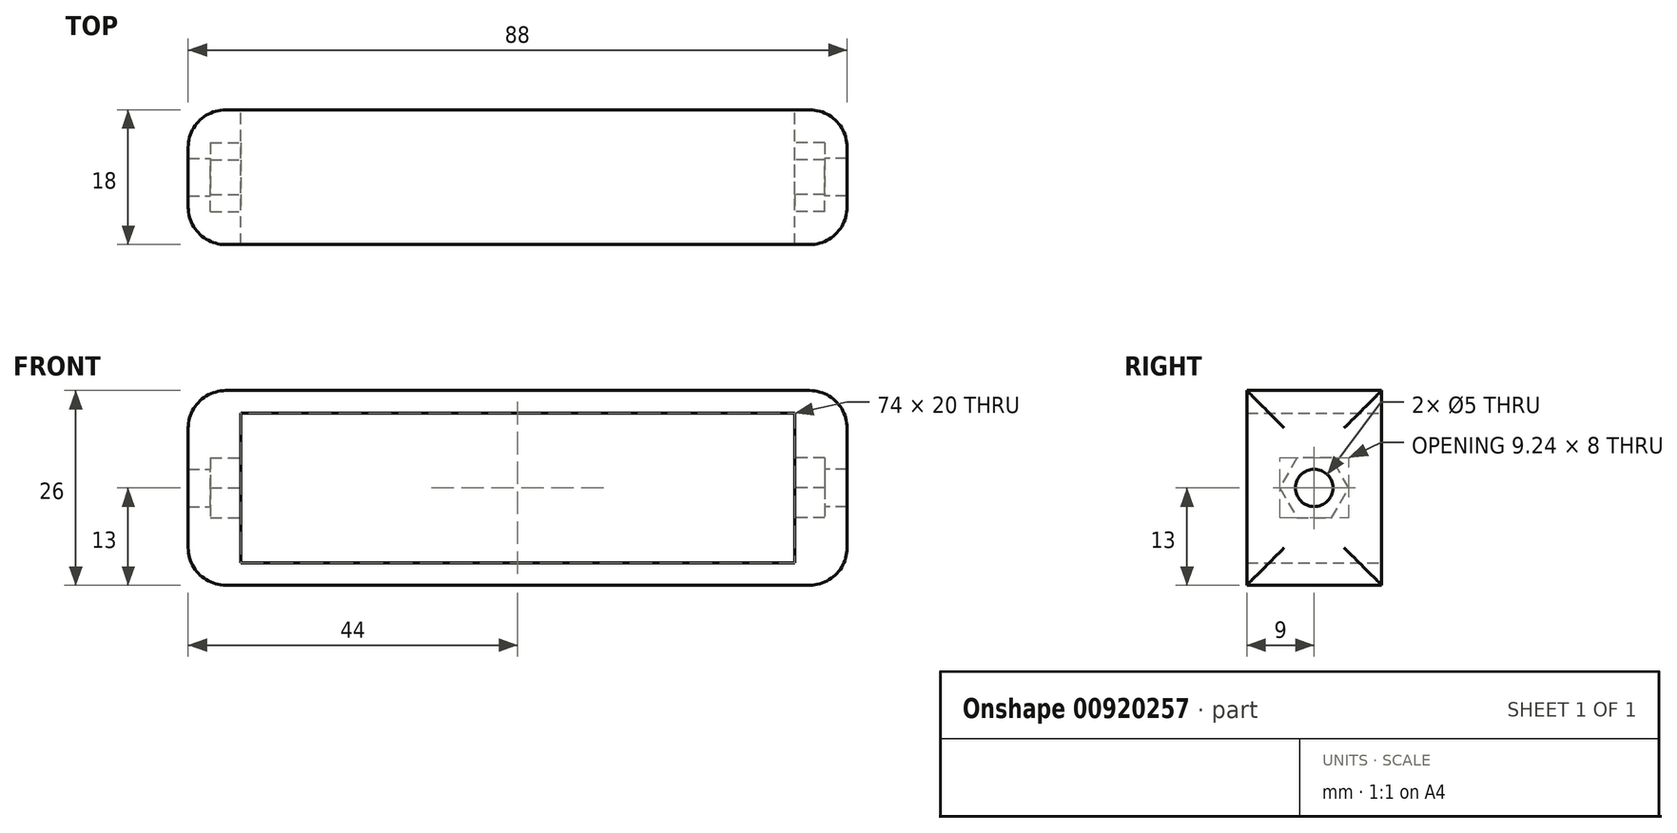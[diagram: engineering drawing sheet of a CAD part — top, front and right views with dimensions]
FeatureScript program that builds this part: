
annotation { "Feature Type Name" : "Feature", "Feature Type Description" : "" }
export const myFeature = defineFeature(function(context is Context, id is Id, definition is map)
    precondition{}
    {
        {
            var Q0;
            Q0=qCreatedBy(makeId("Top.planeOp"),FACE);
            var sketch = newSketch(context, id + "F0", { "sketchPlane" : qUnion([Q0])});
            skLineSegment(sketch, "E0.bottom", {"start": v(44, -9) * mm, "end": v(-44, -9) * mm});
            skLineSegment(sketch, "E0.top", {"start": v(44, 9) * mm, "end": v(-44, 9) * mm});
            skLineSegment(sketch, "E0.left", {"start": v(44, -9) * mm, "end": v(44, 9) * mm});
            skLineSegment(sketch, "E0.right", {"start": v(-44, -9) * mm, "end": v(-44, 9) * mm});
            skPoint(sketch, "E0.middle", {"position": v(0, 0) * mm});
            skSolve(sketch);
        }
        {
            var Q0;
            Q0 = qSketchRegion(id + "F0", true);
            extrude(context, id + "F1", {"entities" : qUnion([Q0]), "depth" : 23 * mm, "offsetDistance" : 25 * mm});
        }
        {
            var Q0;
            Q0=makeQuery(id+"F1.opExtrude","CAP_FACE",FACE,{"disambiguationData":[OSD([sQuery(id+"F0.wireOp",EDGE,"E0.bottom"),sQuery(id+"F0.wireOp",EDGE,"E0.top"),sQuery(id+"F0.wireOp",EDGE,"E0.left"),sQuery(id+"F0.wireOp",EDGE,"E0.right")])],"isStart":false});
            var sketch = newSketch(context, id + "F2", { "sketchPlane" : qUnion([Q0])});
            skLineSegment(sketch, "E1.bottom", {"start": v(37, -9) * mm, "end": v(-37, -9) * mm});
            skLineSegment(sketch, "E1.top", {"start": v(37, 9) * mm, "end": v(-37, 9) * mm});
            skLineSegment(sketch, "E1.left", {"start": v(37, -9) * mm, "end": v(37, 9) * mm});
            skLineSegment(sketch, "E1.right", {"start": v(-37, -9) * mm, "end": v(-37, 9) * mm});
            skPoint(sketch, "E1.middle", {"position": v(0, 0) * mm});
            skSolve(sketch);
        }
        {
            var Q0;
            Q0 = qSketchRegion(id + "F2", true);
            extrude(context, id + "F3", {"entities" : qUnion([Q0]), "operationType" : NewBodyOperationType.REMOVE, "oppositeDirection" : true, "depth" : 20 * mm, "offsetDistance" : 25 * mm});
        }
        {
            var Q0;
            Q0=makeQuery(id+"F3.boolean.opBoolean","COPY",FACE,{"derivedFrom":makeQuery(id+"F3.opExtrude","SWEPT_FACE",FACE,{"disambiguationData":[OSD([sQuery(id+"F2.wireOp",EDGE,"E1.right")])]})});
            var sketch = newSketch(context, id + "F4", { "sketchPlane" : qUnion([Q0])});
            skCircle(sketch, "E2.cCircle", {"center": v(0, 13) * mm, "radius": 4 * mm, "construction": true});
            skPoint(sketch, "E2.cCircle.centerSnap0", {"position": v(0, 23) * mm});
            skPoint(sketch, "E2.cCircle.centerSnap1", {"position": v(-9, 13) * mm});
            skLineSegment(sketch, "E2.0", {"start": v(2.3, 9) * mm, "end": v(-2.3, 9) * mm});
            skLineSegment(sketch, "E2.1", {"start": v(-2.3, 9) * mm, "end": v(-4.62, 13) * mm});
            skLineSegment(sketch, "E2.2", {"start": v(-4.62, 13) * mm, "end": v(-2.3, 17) * mm});
            skLineSegment(sketch, "E2.3", {"start": v(-2.3, 17) * mm, "end": v(2.3, 17) * mm});
            skLineSegment(sketch, "E2.4", {"start": v(2.3, 17) * mm, "end": v(4.62, 13) * mm});
            skLineSegment(sketch, "E2.5", {"start": v(4.62, 13) * mm, "end": v(2.3, 9) * mm});
            skPoint(sketch, "E2.0.midPoint", {"position": v(0, 9) * mm});
            skSolve(sketch);
        }
        {
            var Q0;
            Q0 = qSketchRegion(id + "F4", true);
            extrude(context, id + "F5", {"entities" : qUnion([Q0]), "operationType" : NewBodyOperationType.REMOVE, "oppositeDirection" : true, "depth" : 4 * mm, "offsetDistance" : 25 * mm});
        }
        {
            var Q0;
            Q0=makeQuery(id+"F3.boolean.opBoolean","COPY",FACE,{"derivedFrom":makeQuery(id+"F3.opExtrude","SWEPT_FACE",FACE,{"disambiguationData":[OSD([sQuery(id+"F2.wireOp",EDGE,"E1.left")])]})});
            var sketch = newSketch(context, id + "F6", { "sketchPlane" : qUnion([Q0])});
            skCircle(sketch, "E3.cCircle", {"center": v(0, 13) * mm, "radius": 4 * mm, "construction": true});
            skPoint(sketch, "E3.cCircle.centerSnap0", {"position": v(-9, 13) * mm});
            skPoint(sketch, "E3.cCircle.centerSnap1", {"position": v(0, 23) * mm});
            skLineSegment(sketch, "E3.0", {"start": v(2.3, 9) * mm, "end": v(-2.3, 9) * mm});
            skLineSegment(sketch, "E3.1", {"start": v(-2.3, 9) * mm, "end": v(-4.62, 13) * mm});
            skLineSegment(sketch, "E3.2", {"start": v(-4.62, 13) * mm, "end": v(-2.3, 17) * mm});
            skLineSegment(sketch, "E3.3", {"start": v(-2.3, 17) * mm, "end": v(2.3, 17) * mm});
            skLineSegment(sketch, "E3.4", {"start": v(2.3, 17) * mm, "end": v(4.62, 13) * mm});
            skLineSegment(sketch, "E3.5", {"start": v(4.62, 13) * mm, "end": v(2.3, 9) * mm});
            skPoint(sketch, "E3.0.midPoint", {"position": v(0, 9) * mm});
            skSolve(sketch);
        }
        {
            var Q0;
            Q0 = qSketchRegion(id + "F6", true);
            extrude(context, id + "F7", {"entities" : qUnion([Q0]), "operationType" : NewBodyOperationType.REMOVE, "oppositeDirection" : true, "depth" : 4 * mm, "offsetDistance" : 25 * mm});
        }
        {
            var Q0;
            Q0=makeQuery(id+"F7.boolean.opBoolean","COPY",FACE,{"derivedFrom":makeQuery(id+"F7.opExtrude","CAP_FACE",FACE,{"disambiguationData":[OSD([sQuery(id+"F6.wireOp",EDGE,"E3.0"),sQuery(id+"F6.wireOp",EDGE,"E3.1"),sQuery(id+"F6.wireOp",EDGE,"E3.2"),sQuery(id+"F6.wireOp",EDGE,"E3.3"),sQuery(id+"F6.wireOp",EDGE,"E3.4"),sQuery(id+"F6.wireOp",EDGE,"E3.5")])],"isStart":false})});
            var sketch = newSketch(context, id + "F8", { "sketchPlane" : qUnion([Q0])});
            skCircle(sketch, "E4", {"center": v(0, 13) * mm, "radius": 2.5 * mm});
            skPoint(sketch, "E4.centerSnap0", {"position": v(0, 9) * mm});
            skSolve(sketch);
        }
        {
            var Q0;
            Q0 = qSketchRegion(id + "F8", true);
            extrude(context, id + "F9", {"entities" : qUnion([Q0]), "operationType" : NewBodyOperationType.REMOVE, "endBound" : BoundingType.UP_TO_NEXT, "oppositeDirection" : true, "depth" : 25 * mm, "offsetDistance" : 25 * mm});
        }
        {
            var Q0;
            Q0=makeQuery(id+"F5.boolean.opBoolean","COPY",FACE,{"derivedFrom":makeQuery(id+"F5.opExtrude","CAP_FACE",FACE,{"disambiguationData":[OSD([sQuery(id+"F4.wireOp",EDGE,"E2.0"),sQuery(id+"F4.wireOp",EDGE,"E2.1"),sQuery(id+"F4.wireOp",EDGE,"E2.2"),sQuery(id+"F4.wireOp",EDGE,"E2.3"),sQuery(id+"F4.wireOp",EDGE,"E2.4"),sQuery(id+"F4.wireOp",EDGE,"E2.5")])],"isStart":false})});
            var sketch = newSketch(context, id + "F10", { "sketchPlane" : qUnion([Q0])});
            skCircle(sketch, "E5", {"center": v(0, 13) * mm, "radius": 2.5 * mm});
            skPoint(sketch, "E5.centerSnap0", {"position": v(0, 17) * mm});
            skSolve(sketch);
        }
        {
            var Q0;
            Q0 = qSketchRegion(id + "F10", true);
            extrude(context, id + "F11", {"entities" : qUnion([Q0]), "operationType" : NewBodyOperationType.REMOVE, "endBound" : BoundingType.UP_TO_NEXT, "oppositeDirection" : true, "depth" : 25 * mm, "offsetDistance" : 25 * mm});
        }
        {
            var Q0;
            {var subQ0=sQuery(id+"F0.wireOp",EDGE,"E0.bottom");var subQ1=sQuery(id+"F0.wireOp",EDGE,"E0.right");var subQ2=sQuery(id+"F0.wireOp",EDGE,"E0.top");Q0=makeQuery(id+"F3.boolean.opBoolean","SPLIT",FACE,{"disambiguationData":[TD([makeQuery(id+"F1.opExtrude","SWEPT_FACE",FACE,{"disambiguationData":[OSD([subQ1])]})])],"derivedFrom":makeQuery(id+"F1.opExtrude","CAP_FACE",FACE,{"disambiguationData":[OSD([subQ0,subQ2,sQuery(id+"F0.wireOp",EDGE,"E0.left"),subQ1])],"isStart":false})});}
            var sketch = newSketch(context, id + "F12", { "sketchPlane" : qUnion([Q0])});
            skLineSegment(sketch, "E6.bottom", {"start": v(-44, 9) * mm, "end": v(44, 9) * mm});
            skLineSegment(sketch, "E6.top", {"start": v(-44, -9) * mm, "end": v(44, -9) * mm});
            skLineSegment(sketch, "E6.left", {"start": v(-44, 9) * mm, "end": v(-44, -9) * mm});
            skLineSegment(sketch, "E6.right", {"start": v(44, 9) * mm, "end": v(44, -9) * mm});
            skSolve(sketch);
        }
        {
            var Q0;
            Q0 = qSketchRegion(id + "F12", true);
            extrude(context, id + "F13", {"entities" : qUnion([Q0]), "depth" : 3 * mm, "offsetDistance" : 25 * mm});
        }
        {
            var Q0;
            Q0=makeQuery(id+"F1.opExtrude","SWEPT_BODY",BODY,{"disambiguationData":[OSD([sQuery(id+"F0.wireOp",EDGE,"E0.bottom"),sQuery(id+"F0.wireOp",EDGE,"E0.top"),sQuery(id+"F0.wireOp",EDGE,"E0.left"),sQuery(id+"F0.wireOp",EDGE,"E0.right")])]});
            var Q1;
            Q1=makeQuery(id+"F13.opExtrude","SWEPT_BODY",BODY,{"disambiguationData":[OSD([sQuery(id+"F12.wireOp",EDGE,"E6.bottom"),sQuery(id+"F12.wireOp",EDGE,"E6.top"),sQuery(id+"F12.wireOp",EDGE,"E6.left"),sQuery(id+"F12.wireOp",EDGE,"E6.right")])]});
            booleanBodies(context, id + "F14", {"operationType" : BooleanOperationType.UNION, "tools" : qUnion([Q0, Q1])});
        }
        {
            var Q0;
            Q0=makeQuery(id+"F13.opExtrude","CAP_EDGE",EDGE,{"disambiguationData":[OSD([sQuery(id+"F12.wireOp",EDGE,"E6.left")])],"isStart":false});
            var Q1;
            Q1=makeQuery(id+"F1.opExtrude","CAP_EDGE",EDGE,{"disambiguationData":[OSD([sQuery(id+"F0.wireOp",EDGE,"E0.right")])],"isStart":true});
            var Q2;
            Q2=makeQuery(id+"F13.opExtrude","CAP_EDGE",EDGE,{"disambiguationData":[OSD([sQuery(id+"F12.wireOp",EDGE,"E6.right")])],"isStart":false});
            var Q3;
            Q3=makeQuery(id+"F1.opExtrude","CAP_EDGE",EDGE,{"disambiguationData":[OSD([sQuery(id+"F0.wireOp",EDGE,"E0.left")])],"isStart":true});
            var Q4;
            Q4=makeQuery(id+"F14.opBoolean","MERGE",EDGE,{"derivedFrom":[makeQuery(id+"F1.opExtrude","SWEPT_EDGE",EDGE,{"disambiguationData":[OSD([sQuery(id+"F0.wireOp",EDGE,"E0.bottom"),sQuery(id+"F0.wireOp",EDGE,"E0.right")])]}),makeQuery(id+"F13.opExtrude","SWEPT_EDGE",EDGE,{"disambiguationData":[OSD([sQuery(id+"F12.wireOp",EDGE,"E6.top"),sQuery(id+"F12.wireOp",EDGE,"E6.left")])]})]});
            var Q5;
            Q5=makeQuery(id+"F14.opBoolean","MERGE",EDGE,{"derivedFrom":[makeQuery(id+"F1.opExtrude","SWEPT_EDGE",EDGE,{"disambiguationData":[OSD([sQuery(id+"F0.wireOp",EDGE,"E0.top"),sQuery(id+"F0.wireOp",EDGE,"E0.right")])]}),makeQuery(id+"F13.opExtrude","SWEPT_EDGE",EDGE,{"disambiguationData":[OSD([sQuery(id+"F12.wireOp",EDGE,"E6.bottom"),sQuery(id+"F12.wireOp",EDGE,"E6.left")])]})]});
            var Q6;
            Q6=makeQuery(id+"F14.opBoolean","MERGE",EDGE,{"derivedFrom":[makeQuery(id+"F1.opExtrude","SWEPT_EDGE",EDGE,{"disambiguationData":[OSD([sQuery(id+"F0.wireOp",EDGE,"E0.bottom"),sQuery(id+"F0.wireOp",EDGE,"E0.left")])]}),makeQuery(id+"F13.opExtrude","SWEPT_EDGE",EDGE,{"disambiguationData":[OSD([sQuery(id+"F12.wireOp",EDGE,"E6.top"),sQuery(id+"F12.wireOp",EDGE,"E6.right")])]})]});
            var Q7;
            Q7=makeQuery(id+"F14.opBoolean","MERGE",EDGE,{"derivedFrom":[makeQuery(id+"F1.opExtrude","SWEPT_EDGE",EDGE,{"disambiguationData":[OSD([sQuery(id+"F0.wireOp",EDGE,"E0.top"),sQuery(id+"F0.wireOp",EDGE,"E0.left")])]}),makeQuery(id+"F13.opExtrude","SWEPT_EDGE",EDGE,{"disambiguationData":[OSD([sQuery(id+"F12.wireOp",EDGE,"E6.bottom"),sQuery(id+"F12.wireOp",EDGE,"E6.right")])]})]});
            fillet(context, id + "F15", {"entities" : qUnion([Q0, Q1, Q2, Q3, Q4, Q5, Q6, Q7]), "radius" : 5 * mm, "tangentPropagation" : true, "allowEdgeOverflow" : false});
        }
    });
